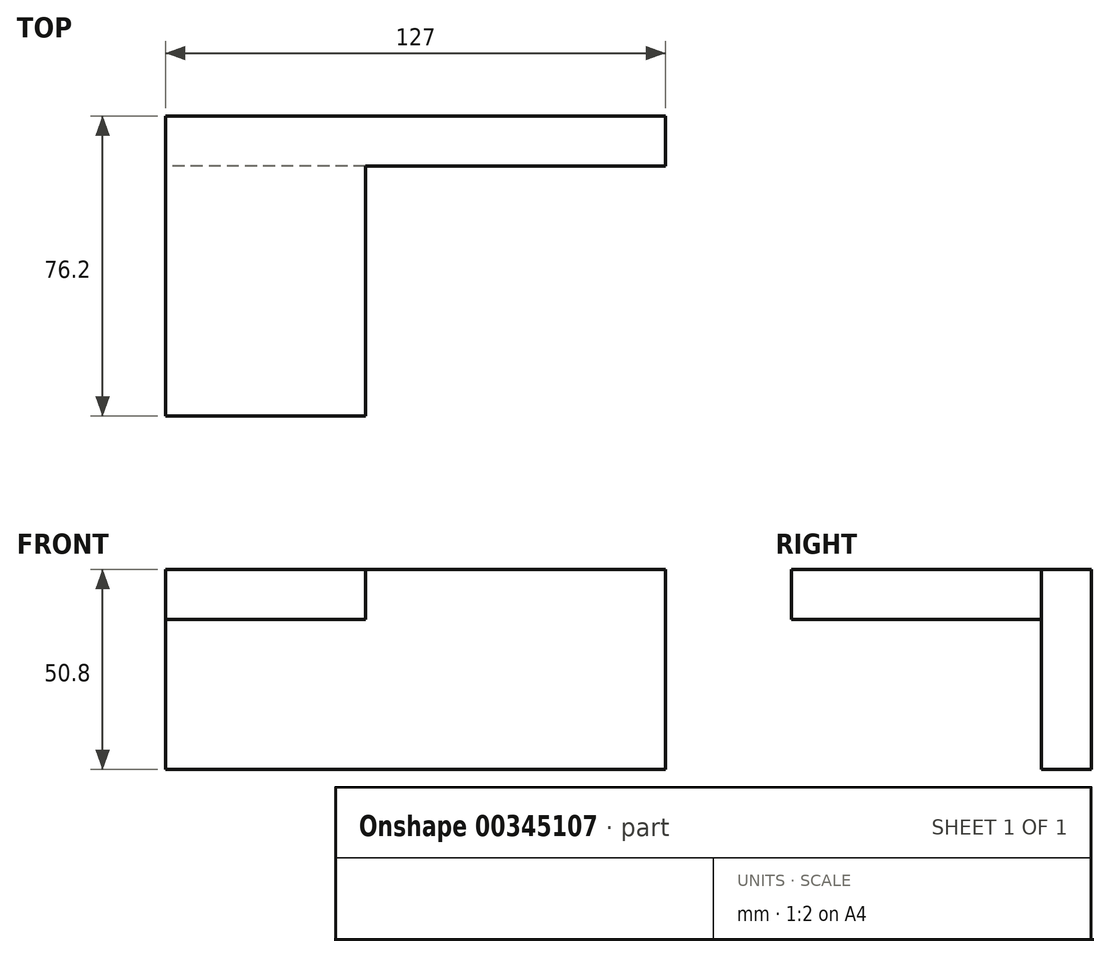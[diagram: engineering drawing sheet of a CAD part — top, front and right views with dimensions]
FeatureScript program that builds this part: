
annotation { "Feature Type Name" : "Feature", "Feature Type Description" : "" }
export const myFeature = defineFeature(function(context is Context, id is Id, definition is map)
    precondition{}
    {
        {
            var Q0;
            Q0=qCreatedBy(makeId("Right.planeOp"),FACE);
            var sketch = newSketch(context, id + "F0", { "sketchPlane" : qUnion([Q0])});
            skLineSegment(sketch, "E0", {"start": v(0, 0) * mm, "end": v(0, 50.8) * mm});
            skLineSegment(sketch, "E1", {"start": v(0, 50.8) * mm, "end": v(-76.2, 50.8) * mm});
            skLineSegment(sketch, "E2", {"start": v(-76.2, 50.8) * mm, "end": v(-76.2, 38.1) * mm});
            skLineSegment(sketch, "E3", {"start": v(-76.2, 38.1) * mm, "end": v(-12.7, 38.1) * mm});
            skLineSegment(sketch, "E4", {"start": v(-12.7, 38.1) * mm, "end": v(-12.7, 0) * mm});
            skLineSegment(sketch, "E5", {"start": v(-12.7, 0) * mm, "end": v(0, 0) * mm});
            skSolve(sketch);
        }
        {
            var Q0;
            Q0 = qSketchRegion(id + "F0", true);
            extrude(context, id + "F1", {"entities" : qUnion([Q0]), "depth" : 127 * mm});
        }
        {
            var Q0;
            Q0=makeQuery(id+"F1.opExtrude","SWEPT_FACE",FACE,{"disambiguationData":[OSD([sQuery(id+"F0.wireOp",EDGE,"E1")])]});
            var sketch = newSketch(context, id + "F2", { "sketchPlane" : qUnion([Q0])});
            skLineSegment(sketch, "E6.bottom", {"start": v(127, -76.2) * mm, "end": v(50.8, -76.2) * mm});
            skLineSegment(sketch, "E6.top", {"start": v(127, -12.7) * mm, "end": v(50.8, -12.7) * mm});
            skLineSegment(sketch, "E6.left", {"start": v(127, -76.2) * mm, "end": v(127, -12.7) * mm});
            skLineSegment(sketch, "E6.right", {"start": v(50.8, -76.2) * mm, "end": v(50.8, -12.7) * mm});
            skSolve(sketch);
        }
        {
            var Q0;
            Q0=makeQuery(id+"F2.imprint","IMPRINT",FACE,{"disambiguationData":[TD([[makeQuery(id+"F2.imprint","IMPRINT",EDGE,{"derivedFrom":sQuery(id+"F2.wireOp",EDGE,"E6.bottom")}),-1.0]])]});
            var Q1;
            Q1=sQuery(id+"F2.wireOp",EDGE,"E6.top");
            extrude(context, id + "F3", {"entities" : qUnion([Q0]), "operationType" : NewBodyOperationType.REMOVE, "surfaceEntities" : qUnion([Q1]), "oppositeDirection" : true, "depth" : 25.4 * mm});
        }
    });
